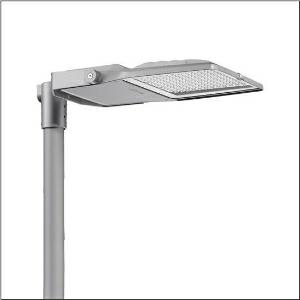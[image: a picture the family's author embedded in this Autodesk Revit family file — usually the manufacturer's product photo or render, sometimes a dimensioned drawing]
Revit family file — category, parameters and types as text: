
# Revit family: floodlight_fl_21_iq_midi___pl64_5xa7782e2e3a_fffa
name_source: partatom
category: Lighting Fixtures
units: mm (PartAtom-declared; Revit-internal decimal feet)

## family parameters
Cut with Voids When Loaded = No
Host = Face
Light Source = No
Part Type = Normal
Room Calculation Point = No
Round Connector Dimension = Use Diameter
Shared = No

## types (1)
- --- (1 x LED, 25930 lm, 208.1 W, 3000K)
    Apparent Load = 208 VA
    CIE Flux Codes = 28 80 98 100 100
    Color Rendering = 70
    Color Temperature = 3000K
    Default Elevation = 1800 mm
    Description = Floodlight FL 21 iQ midi, floodlight, primary light control with lens, of PMMA, primary optical cover: protective disc, of toughened safety glass, transparent, light distribution: PL64, light emission: direct distribution, installation type: surface-mounted, LED, High Power LED, rated luminous flux: 25.930lm, luminous efficacy: 125lm/W, light colour: 730, colour temperature: 3000K, control gear: iQ Street-Remote/DALI, control: optimised constant luminous flux control (CLO 2.0), Desk-Remote (wireless, voltage-free reading and setting of iQ features in the workshop via application-optimized NFC function/RFID function), Smart-Wire, Night-Set, Temp-Guard, Auto-Match, Street-Remote, with terminal, 6-pole, mains connection: 220..240V, AC, 50/60Hz, start of lifetime: 208W, end of service life: 227W, reduction: 90W, luminaire housing, of diecast aluminium, powder-coated, Siteco® metallic grey (DB 702S), corrosivity category C5 mid according to DIN EN ISO 12944, suitable for swimming pools, chlorine-resistant, sealing non-destructively replaceable, please order mast flange separately, mast bracket, of steel, galvanised, powder-coated, Siteco® metallic grey (DB 702S), protection rating (complete): IP66, insulation class (complete): insulation class II (safety insulation), certification: CE, ENEC, VDE, protection symbol: D, impact resistance: IK08, permissible operating ambient temperature: -40..+40°C, permissible operating ambient temperature for outdoor applications: -40..+50°C, standard: DIN EN 12944, LABS conformity tested according to VDMA 24364:2018-05, packaging unit: 1 piece

Light Distribution: PL64
    Height = 76 mm
    Lamp = 1 x LED
    Lamp Light Flux = 25930 lm
    Lamp Power = 208.1 W
    Lamp count = 1
    Length = 657 mm
    Luminous efficacy = 125 lm/W
    Manufacturer = Siteco
    ModVariant = No
    Model = 5XA7782E2E3A
    Number of Poles = 1
    OnlyDefault = Yes
    Power Factor = 1
    Product Name = Floodlight FL 21 iQ midi | PL64
    Product group = floodlight | pylon annexe
    ProductGroupID = 6200
    Protection Class = Protection class II
    Protection Degree = IP 66
    RLX_Detail_Level = 1
    RLX_Emergency_Light_Flux = 0 lm
    RLX_Emergency_Type = 0
    RLX_Emergency_Type_DB = No
    RlxData = <blob elided: 153617 chars, md5=3bdf6768>
    Socket = socket
    Standby Power = 0 W
    System Light Flux = 25930 lm
    System Power = 208 W
    Type Comments = factory setting: luminous flux: 100 % | dim-lin: 254 | 710 mA
    Type Image = l_1007123.jpg
    URL = http://relux.com
    VarID = @adj_107096
    Voltage = 0 V
    Weight = 0.00 kg
    Width = 442 mm

## geometry (parser evidence)
native form markers: Blend x4, Sweep x13
no freeform markers — native parametric forms only
